# Revit family: EU-2015_Door_Klein_Lite+100-KSC
name_source: partatom
category: Doors
revit_build: Autodesk Revit 2015 (Build: 20160512_1515(x64)
units: mm (PartAtom-declared; Revit-internal decimal feet)

## types (1)
- EU-2015_Door_Klein_Lite+100-KSC
    BIMElementExpiryDate = 13/11/2018
    BIMElementIssueDate = 13/11/2017
    BIMElementVersion = V01
    Bimetica = www.bimetica.com
    Description = Sliding Glass Door
    EmbodiedCarbon = 0
    End Caps = Acetal Resin-White
    EnergeticCostKw·h = 0
    EnergeticCostMJ = 0 J
    FireExit = No
    Frame Material = Aluminium, Anodized Silver
    Function = Interior
    GlazingAreaFraction = 0.00%
    HandicapAccessible = No
    Handle Height = 850 mm  [stored 2.78871 ft]
    HasDrive = No
    Height = 2100 mm
    IFCClassification = IfcDoor
    IsExternal = No
    MaintenanceCost = 0
    Manufacturer = Klein
    MasterformatCode = 08 12 16
    MasterformatTitle = Aluminum Frames
    Model = Lite+
    OmniclassCode = 23-17 11 23 13
    OmniclassTitle = Sliding All Glass Doors
    Panel Material = Birch, Natural
    ProductURL = http://www.klein-europe.com
    RawMaterial = 0.00%
    Reference = LITE+ 100 KSC Retrac
    Rough Height = 0 mm  [stored 0 ft]
    Rough Width = 1070 mm  [stored 3.5105 ft]
    SmokeStop = No
    SurfaceMass = 0
    TechnicalInformation = http://www.klein-europe.com
    Thickness = 30 mm  [stored 0.0984252 ft]
    True Thickness = 30 mm  [stored 0.0984252 ft]
    Type Comments = Door maximum weight up to 100Kg. All dimensions must be checked with KLEIN mounting instructions. The system is available in Silver, Black or Dark Bronze anodized finish. KSC optional (Klein Soft Closing) for a smooth and controlled closing for glass width starting at 750mm. Check the feasibility of the system on our Website.
    UNSPSCCode = 30162306
    UNSPSCTitle = Door mount or sliding towel hardware or assembly
    URL = http://www.klein-europe.com
    Uniclass2.0Code = 30-59-23-02
    Uniclass2.0Title = Aluminium door frames
    Wall Closure = By host
    Width = 800 mm  [stored 2.62467 ft]

note: [stored X ft] marks values corroborated as IEEE doubles in the binary element streams (Revit-internal decimal feet)

## geometry (parser evidence)
native form markers: Sweep x4
no freeform markers — native parametric forms only
